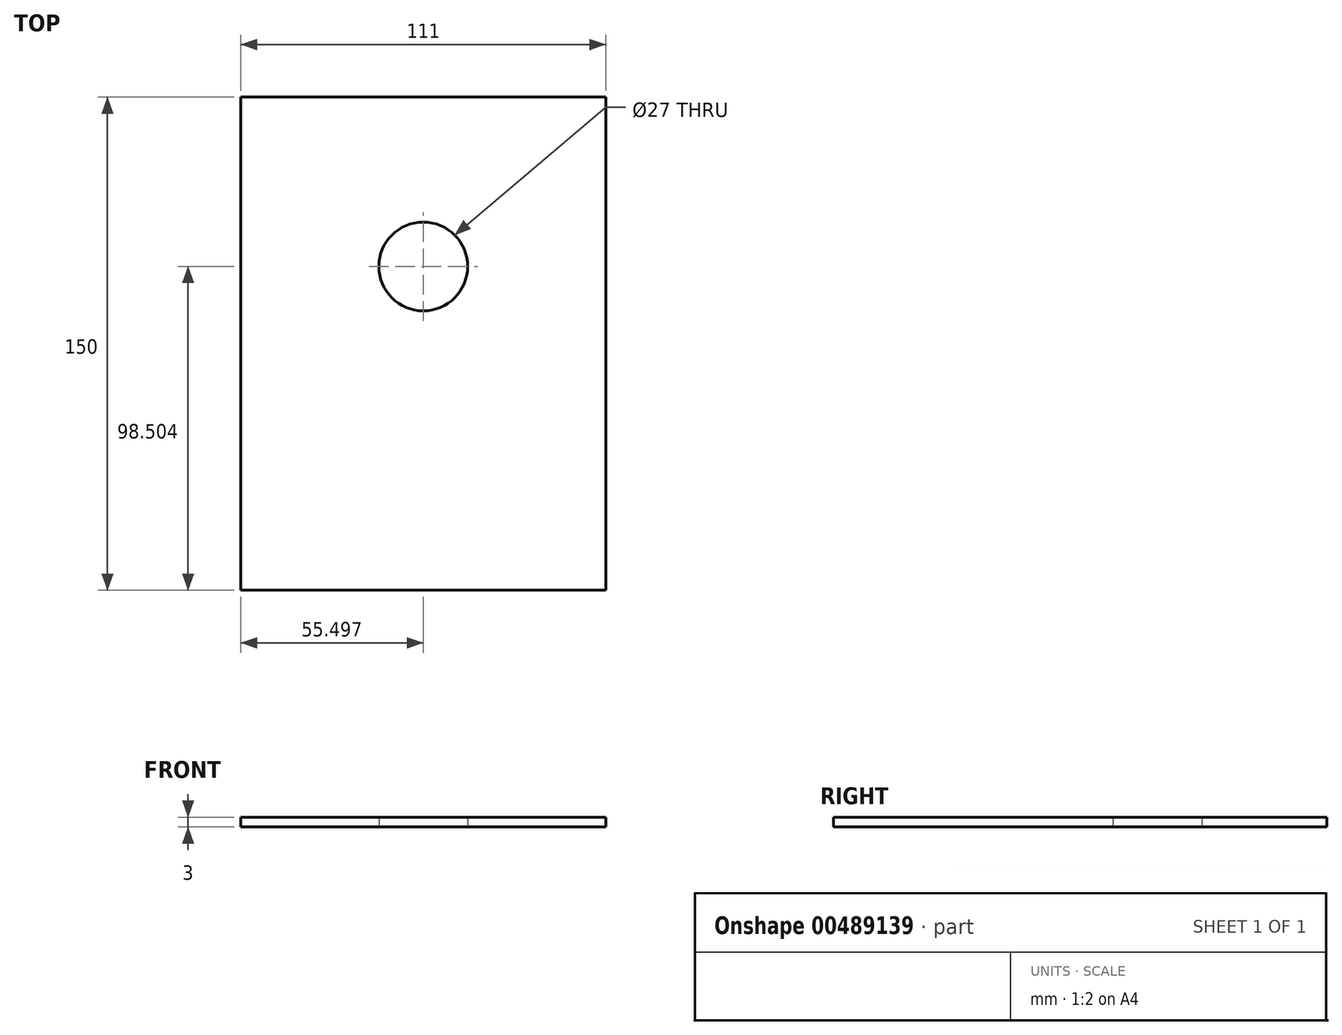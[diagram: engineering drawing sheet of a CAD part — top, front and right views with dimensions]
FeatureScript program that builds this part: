
annotation { "Feature Type Name" : "Feature", "Feature Type Description" : "" }
export const myFeature = defineFeature(function(context is Context, id is Id, definition is map)
    precondition{}
    {
        {
            var Q0;
            Q0=qCreatedBy(makeId("Top.planeOp"),FACE);
            var sketch = newSketch(context, id + "F0", { "sketchPlane" : qUnion([Q0])});
            skLineSegment(sketch, "E0.bottom", {"start": v(-55.7, 40.54) * mm, "end": v(55.3, 40.54) * mm});
            skLineSegment(sketch, "E0.top", {"start": v(-55.7, -109.46) * mm, "end": v(55.3, -109.46) * mm});
            skLineSegment(sketch, "E0.left", {"start": v(-55.7, 40.54) * mm, "end": v(-55.7, -109.46) * mm});
            skLineSegment(sketch, "E0.right", {"start": v(55.3, 40.54) * mm, "end": v(55.3, -109.46) * mm});
            skCircle(sketch, "E1", {"center": v(-0.2, -10.96) * mm, "radius": 13.5 * mm});
            skSolve(sketch);
        }
        {
            var Q0;
            Q0=makeQuery(id+"F0.imprint","IMPRINT",FACE,{"disambiguationData":[TD([[makeQuery(id+"F0.imprint","IMPRINT",EDGE,{"derivedFrom":sQuery(id+"F0.wireOp",EDGE,"E0.bottom")}),-1.0]])]});
            extrude(context, id + "F1", {"entities" : qUnion([Q0]), "flatOperationType" : FlatOperationType.REMOVE, "offsetDistance" : 25 * mm, "depth" : 3 * mm, "domain" : OperationDomain.MODEL});
        }
    });
